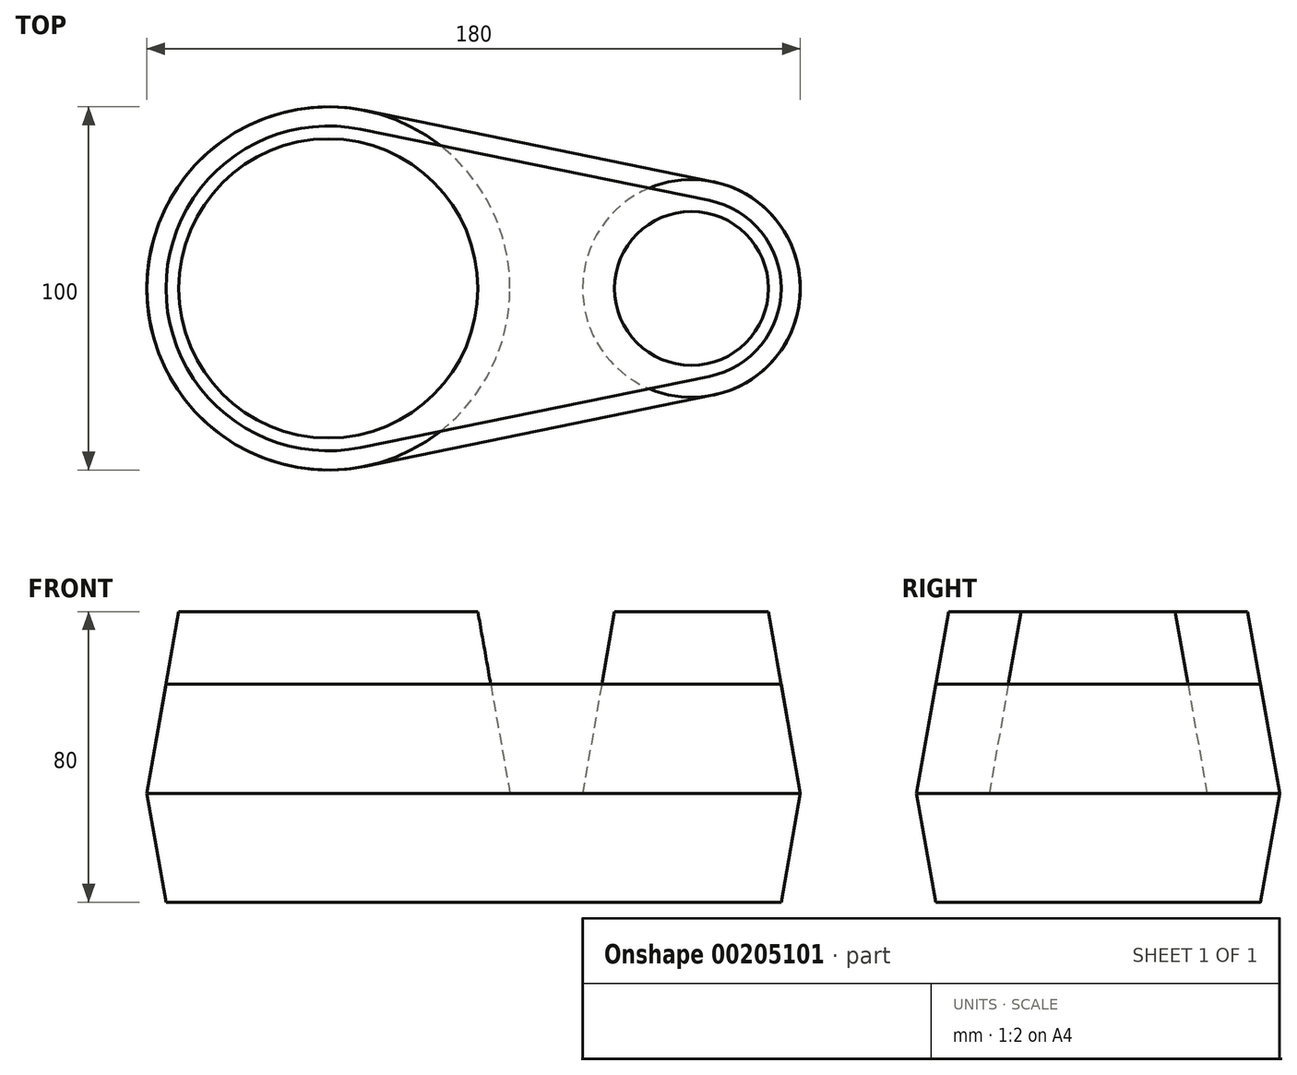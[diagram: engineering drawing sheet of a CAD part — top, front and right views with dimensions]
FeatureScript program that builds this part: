
annotation { "Feature Type Name" : "Feature", "Feature Type Description" : "" }
export const myFeature = defineFeature(function(context is Context, id is Id, definition is map)
    precondition{}
    {
        {
            var Q0;
            Q0=qCreatedBy(makeId("Top.planeOp"),FACE);
            var sketch = newSketch(context, id + "F0", { "sketchPlane" : qUnion([Q0])});
            skCircle(sketch, "E0", {"center": v(0, 0) * mm, "radius": 50 * mm});
            skCircle(sketch, "E1", {"center": v(100, 0) * mm, "radius": 30 * mm});
            skLineSegment(sketch, "E2", {"start": v(10, 48.99) * mm, "end": v(106, 29.4) * mm});
            skLineSegment(sketch, "E3", {"start": v(10, -48.99) * mm, "end": v(106, -29.4) * mm});
            skSolve(sketch);
        }
        {
            var Q0;
            {var subQ0=sQuery(id+"F0.wireOp",EDGE,"E0");var subQ1=makeQuery(id+"F0.imprint","INTERSECT",VERTEX,{"derivedFrom":[subQ0,sQuery(id+"F0.wireOp",EDGE,"E2")]});Q0=makeQuery(id+"F0.imprint","IMPRINT",FACE,{"disambiguationData":[TD([[makeQuery(id+"F0.imprint","IMPRINT",EDGE,{"disambiguationData":[TD([[subQ1,-1.0]])],"derivedFrom":subQ0}),1.0]])]});}
            var Q1;
            {var subQ0=sQuery(id+"F0.wireOp",EDGE,"E1");var subQ1=makeQuery(id+"F0.imprint","INTERSECT",VERTEX,{"derivedFrom":[subQ0,sQuery(id+"F0.wireOp",EDGE,"E2")]});Q1=makeQuery(id+"F0.imprint","IMPRINT",FACE,{"disambiguationData":[TD([[makeQuery(id+"F0.imprint","IMPRINT",EDGE,{"disambiguationData":[TD([[subQ1,-1.0]])],"derivedFrom":subQ0}),1.0]])]});}
            extrude(context, id + "F1", {"entities" : qUnion([Q0, Q1]), "depth" : 50 * mm, "hasDraft" : true, "draftAngle" : 10 * degree, "draftPullDirection" : true});
        }
        {
            var Q0;
            {var subQ0=sQuery(id+"F0.wireOp",EDGE,"E3");Q0=makeQuery(id+"F0.imprint","IMPRINT",FACE,{"disambiguationData":[TD([[makeQuery(id+"F0.imprint","IMPRINT",EDGE,{"derivedFrom":subQ0}),1.0]])]});}
            var Q1;
            {var subQ0=sQuery(id+"F0.wireOp",EDGE,"E2");var subQ1=sQuery(id+"F0.wireOp",EDGE,"E0");var subQ2=makeQuery(id+"F0.imprint","INTERSECT",VERTEX,{"disambiguationData":[OD(0.0)],"derivedFrom":[subQ1,subQ0]});Q1=makeQuery(id+"F0.imprint","IMPRINT",FACE,{"disambiguationData":[TD([[makeQuery(id+"F0.imprint","IMPRINT",EDGE,{"disambiguationData":[TD([[subQ2,-1.0]])],"derivedFrom":subQ1}),1.0]])]});}
            var Q2;
            {var subQ0=sQuery(id+"F0.wireOp",EDGE,"E1");var subQ1=makeQuery(id+"F0.imprint","INTERSECT",VERTEX,{"derivedFrom":[subQ0,sQuery(id+"F0.wireOp",EDGE,"E2")]});Q2=makeQuery(id+"F0.imprint","IMPRINT",FACE,{"disambiguationData":[TD([[makeQuery(id+"F0.imprint","IMPRINT",EDGE,{"disambiguationData":[TD([[subQ1,-1.0]])],"derivedFrom":subQ0}),1.0]])]});}
            extrude(context, id + "F2", {"entities" : qUnion([Q0, Q1, Q2]), "endBound" : BoundingType.SYMMETRIC, "depth" : 60 * mm, "hasDraft" : true, "draftAngle" : 10 * degree, "draftPullDirection" : true});
        }
    });
